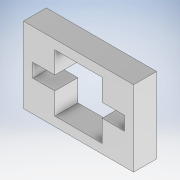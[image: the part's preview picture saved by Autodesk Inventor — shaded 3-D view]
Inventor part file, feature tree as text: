
AUTODESK INVENTOR PART (.ipt)
format: ipt  version: 2018 (Build 220112000, 112)  size: 115,200 bytes
history: native  units: mm
features: extrude x1, chamfer x1, sketch x1
ambient origin geometry x8: Origin, YZ Plane, XZ Plane, XY Plane, X Axis, Y Axis, Z Axis, Center Point
bodies: Solid1 (feature_tree)
feature tree (3):
  extrude  "Extrusion1"  Depth=10.3mm
  chamfer  "Chamfer1"  Distance=12.5mm
  sketch  "Sketch1"  dims[d0=3.0mm d1=10.3mm d2=12.5mm d3=2.0mm d4=2.0mm d5=2.0mm d6=2.0mm d7=20.0mm d8=5.0mm d9=0.0mm d10=1.0mm d11=2.0mm d12=45.0deg]
